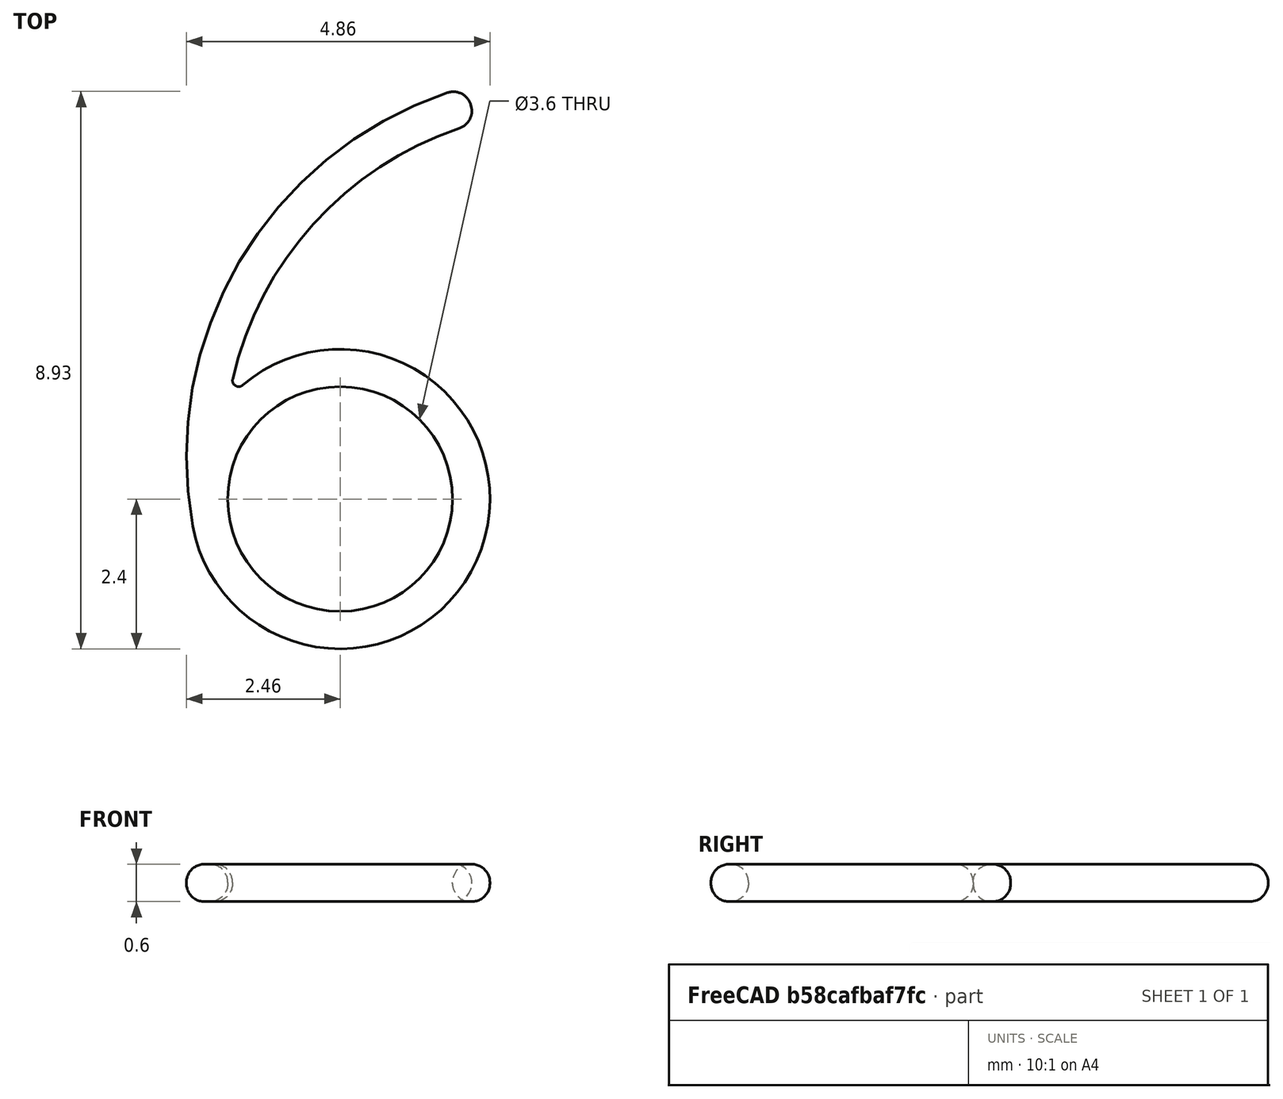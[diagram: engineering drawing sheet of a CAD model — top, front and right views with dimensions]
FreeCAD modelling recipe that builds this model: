
FCSTD DOCUMENT  (FreeCAD 0.16R6712 (Git))
Label: 6s
License: All rights reserved
LicenseURL: http://en.wikipedia.org/wiki/All_rights_reserved
objects: Sketcher::SketchObject×1, PartDesign::Pad×1, PartDesign::Fillet×1, Mesh::Feature×1
note: 4 computed .brp shape members not serialized (recipe doc carries the construction recipe); baked Part::Feature solids carry a one-line shape summary decoded from their .brp

FEATURE [Sketcher::SketchObject] Sketch
  sketch-geometry (6):
    g0: ArcOfCircle CenterX=3.69002 CenterY=3.08076 CenterZ=0 NormalX=0 NormalY=0 NormalZ=1 Radius=6.15229 StartAngle=1.84692 EndAngle=3.32403
    g1: ArcOfCircle CenterX=-1.62405 CenterY=4.30065 CenterZ=0 NormalX=0 NormalY=0 NormalZ=1 Radius=0.1 StartAngle=2.91595 EndAngle=5.4195
    g2: ArcOfCircle CenterX=0 CenterY=2.4 CenterZ=0 NormalX=0 NormalY=0 NormalZ=1 Radius=2.4 StartAngle=3.32403 EndAngle=8.56107
    g3: ArcOfCircle CenterX=3.69002 CenterY=3.08076 CenterZ=0 NormalX=0 NormalY=0 NormalZ=1 Radius=5.55229 StartAngle=1.84692 EndAngle=2.91595
    g4: LineSegment StartX=2.01271 StartY=9 StartZ=0 EndX=2.17629 EndY=8.42273 EndZ=0
    g5: Circle CenterX=0 CenterY=2.4 CenterZ=0 NormalX=0 NormalY=0 NormalZ=1 Radius=1.8
  constraints (17):
    c: Tangent(g0,g2) = -1.5708
    c: Radius(g2) = 2.4
    c: PointOnObject(g2,g-2)
    c: Coincident(g2,g1)
    c: Coincident(g1,g3)
    c: Tangent(g1,g3)
    c: Coincident(g4,g0)
    c: Coincident(g4,g3)
    c: Radius(g1) = 0.1
    c: PointOnObject(g-1,g2)
    c: Radius(g5) = 1.8
    c: Coincident(g2,g5)
    c: DistanceY(g-1,g0) = 9
    c: Coincident(g0,g3)
    c: Perpendicular(g3,g4)
    c: Distance(g3,g0) = 0.6
    c: Tangent(g1,g2)
FEATURE [PartDesign::Pad] Pad
  Length = 0.6
  Length2 = 100
  Midplane = true
  Sketch = -> Sketch
  Type = 0
FEATURE [PartDesign::Fillet] Fillet
  Base = -> Pad [Edge4,Edge7,Edge10,Edge13,Edge15,Edge18,Edge1,Edge11,Edge14,Edge3,Edge6,Edge9,Edge12,Edge17]
  Radius = 0.29
FEATURE [Mesh::Feature] Mesh  label="Fillet (Meshed)"
